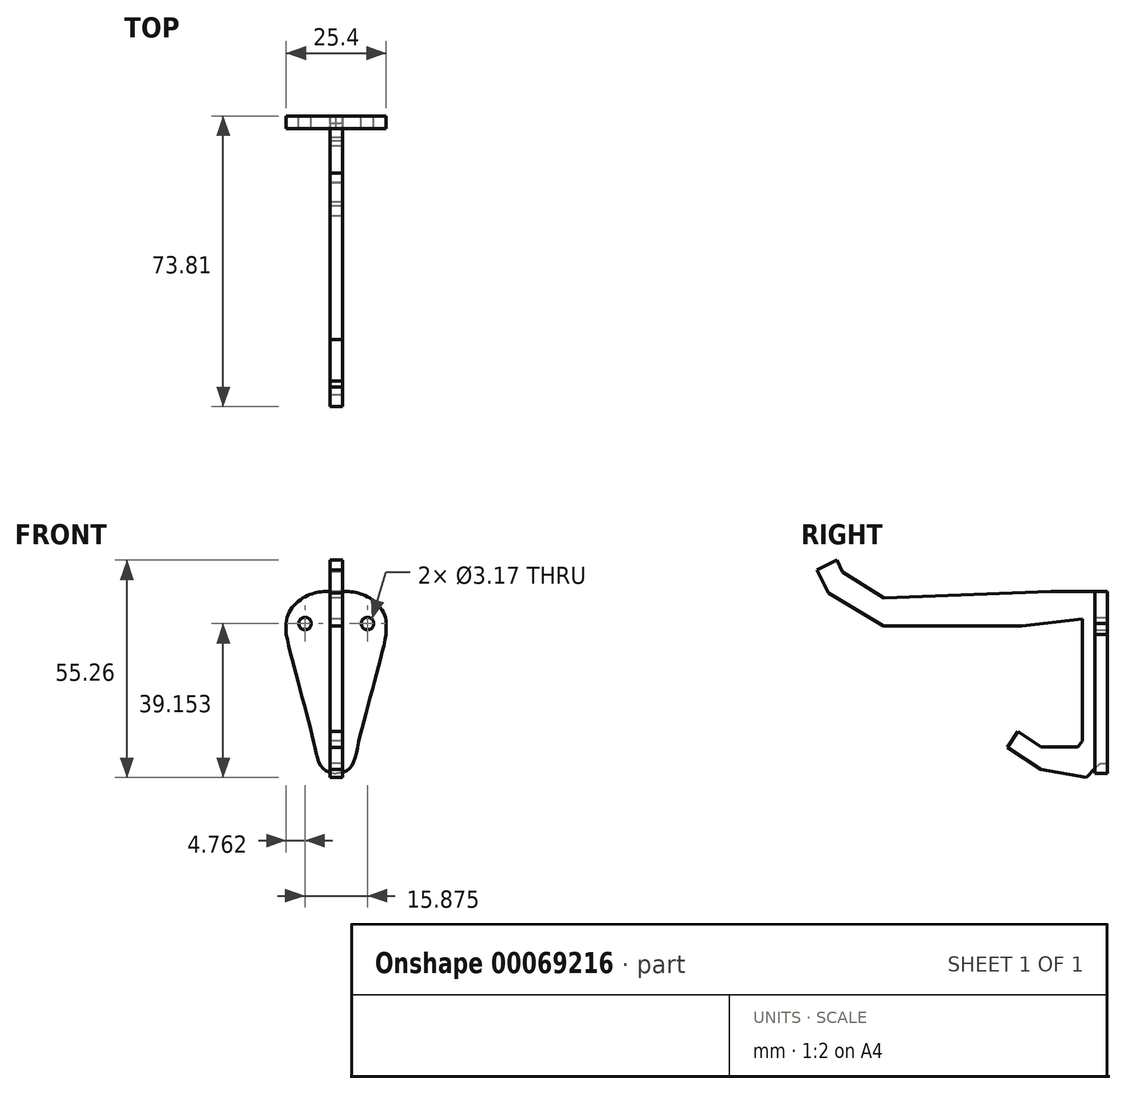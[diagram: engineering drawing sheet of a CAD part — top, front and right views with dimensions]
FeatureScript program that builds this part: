
annotation { "Feature Type Name" : "Feature", "Feature Type Description" : "" }
export const myFeature = defineFeature(function(context is Context, id is Id, definition is map)
    precondition{}
    {
        {
            var Q0;
            Q0=qCreatedBy(makeId("Front.planeOp"),FACE);
            var sketch = newSketch(context, id + "F0", { "sketchPlane" : qUnion([Q0])});
            skLineSegment(sketch, "E0", {"start": v(-12.7, 9.26) * mm, "end": v(-12.7, 6.5) * mm});
            skFitSpline(sketch, "E1", {"points": [v(-12.7, 9.26) * mm, v(-6.7, 16.58) * mm, v(0, 17.38) * mm], "startDerivative": vector(0.72, 20.06) * mm, "endDerivative": vector(13.95, 0.05) * mm});
            skFitSpline(sketch, "E2", {"points": [v(-12.7, 6.5) * mm, v(-5.56, -21.55) * mm, v(0, -28.89) * mm], "startDerivative": vector(5.68, -30.5) * mm, "endDerivative": vector(36.85, -2.9) * mm});
            skFitSpline(sketch, "E3.MirrorCS", {"points": [v(12.7, 9.26) * mm, v(6.7, 16.58) * mm, v(0, 17.38) * mm], "startDerivative": vector(-0.72, 20.06) * mm, "endDerivative": vector(-13.95, 0.05) * mm});
            skLineSegment(sketch, "E4.MirrorCS", {"start": v(12.7, 9.26) * mm, "end": v(12.7, 6.5) * mm});
            skFitSpline(sketch, "E5.MirrorCS", {"points": [v(12.7, 6.5) * mm, v(5.56, -21.55) * mm, v(0, -28.89) * mm], "startDerivative": vector(-5.68, -30.5) * mm, "endDerivative": vector(-36.85, -2.9) * mm});
            skCircle(sketch, "E6", {"center": v(-7.94, 9.21) * mm, "radius": 1.59 * mm});
            skCircle(sketch, "E7", {"center": v(7.94, 9.21) * mm, "radius": 1.59 * mm});
            skSolve(sketch);
        }
        {
            var Q0;
            Q0=qSketchRegion(id+"F0",true);
            extrude(context, id + "F1", {"entities" : qUnion([Q0]), "depth" : 3.17 * mm});
        }
        {
            var Q0;
            Q0=qCreatedBy(makeId("Right.planeOp"),FACE);
            var sketch = newSketch(context, id + "F2", { "sketchPlane" : qUnion([Q0])});
            skLineSegment(sketch, "E8", {"start": v(0, 17.38) * mm, "end": v(-14.4, 17.38) * mm});
            skLineSegment(sketch, "E9", {"start": v(-14.4, 17.38) * mm, "end": v(-56.76, 15.72) * mm});
            skLineSegment(sketch, "E10", {"start": v(-56.76, 15.72) * mm, "end": v(-67.33, 22.32) * mm});
            skLineSegment(sketch, "E11", {"start": v(-67.33, 22.32) * mm, "end": v(-68.8, 25.32) * mm});
            skLineSegment(sketch, "E12", {"start": v(-68.8, 25.32) * mm, "end": v(-73.8, 22.87) * mm});
            skLineSegment(sketch, "E13", {"start": v(-73.8, 22.87) * mm, "end": v(-70.9, 16.93) * mm});
            skLineSegment(sketch, "E14", {"start": v(-70.9, 16.93) * mm, "end": v(-56.95, 8.62) * mm});
            skLineSegment(sketch, "E15", {"start": v(-56.95, 8.62) * mm, "end": v(-21.8, 8.62) * mm});
            skLineSegment(sketch, "E16", {"start": v(-6.35, 10.39) * mm, "end": v(-21.8, 8.62) * mm});
            skLineSegment(sketch, "E17", {"start": v(-6.35, 10.39) * mm, "end": v(-6.35, -20.64) * mm});
            skLineSegment(sketch, "E18", {"start": v(-6.35, -20.64) * mm, "end": v(-7.57, -22.14) * mm});
            skLineSegment(sketch, "E19", {"start": v(-7.57, -22.14) * mm, "end": v(-16.92, -22.14) * mm});
            skLineSegment(sketch, "E20", {"start": v(-16.92, -22.14) * mm, "end": v(-22.82, -18.25) * mm});
            skLineSegment(sketch, "E21", {"start": v(-22.82, -18.25) * mm, "end": v(-25.44, -22.2) * mm});
            skLineSegment(sketch, "E22", {"start": v(-25.44, -22.2) * mm, "end": v(-16.94, -27.81) * mm});
            skLineSegment(sketch, "E23", {"start": v(-16.94, -27.81) * mm, "end": v(-5.4, -29.94) * mm});
            skLineSegment(sketch, "E24", {"start": v(-5.4, -29.94) * mm, "end": v(-1.86, -26.28) * mm});
            skLineSegment(sketch, "E25", {"start": v(-1.86, -26.28) * mm, "end": v(0, -26.28) * mm});
            skLineSegment(sketch, "E26", {"start": v(0, -26.28) * mm, "end": v(0, 17.38) * mm});
            skSolve(sketch);
        }
        {
            var Q0;
            Q0=makeQuery(id+"F2.imprint","IMPRINT",FACE,{"disambiguationData":[TD([[makeQuery(id+"F2.imprint","IMPRINT",EDGE,{"derivedFrom":sQuery(id+"F2.wireOp",EDGE,"E8")}),1.0]])]});
            extrude(context, id + "F3", {"entities" : qUnion([Q0]), "depth" : 1.59 * mm, "hasSecondDirection" : true, "secondDirectionOppositeDirection" : true, "secondDirectionDepth" : 1.59 * mm});
        }
    });
